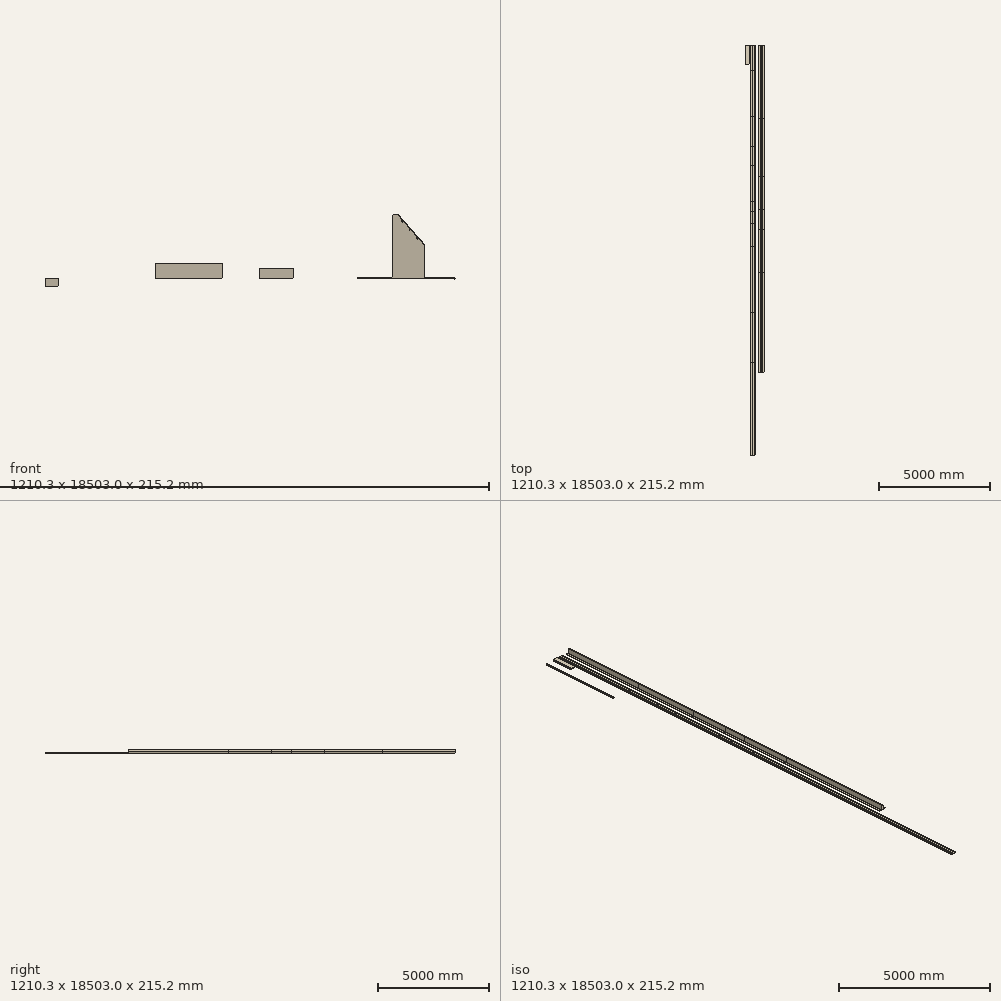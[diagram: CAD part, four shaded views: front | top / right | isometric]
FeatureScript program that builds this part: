
annotation { "Feature Type Name" : "Feature", "Feature Type Description" : "" }
export const myFeature = defineFeature(function(context is Context, id is Id, definition is map)
    precondition{}
    {
        {
            var Q0;
            Q0=qCreatedBy(makeId("Front.planeOp"),FACE);
            var sketch = newSketch(context, id + "F0", { "sketchPlane" : qUnion([Q0])});
            skLineSegment(sketch, "E0", {"start": v(0, 0) * mm, "end": v(105, 0) * mm});
            skLineSegment(sketch, "E1", {"start": v(105, 1) * mm, "end": v(105, 181.45) * mm});
            skLineSegment(sketch, "E2", {"start": v(117.25, 186.07) * mm, "end": v(193, 100) * mm});
            skLineSegment(sketch, "E3", {"start": v(193, 100) * mm, "end": v(193, 0) * mm});
            skLineSegment(sketch, "E4", {"start": v(193, 0) * mm, "end": v(283, 0) * mm});
            skLineSegment(sketch, "E5", {"start": v(283, 0) * mm, "end": v(288, -0.88) * mm});
            skLineSegment(sketch, "E6", {"start": v(288, -0.88) * mm, "end": v(288, 2.12) * mm});
            skLineSegment(sketch, "E7", {"start": v(288, 2.12) * mm, "end": v(283, 3) * mm});
            skLineSegment(sketch, "E8", {"start": v(283, 3) * mm, "end": v(196, 3) * mm});
            skLineSegment(sketch, "E9", {"start": v(196, 3) * mm, "end": v(196, 101.13) * mm});
            skLineSegment(sketch, "E10", {"start": v(196, 101.13) * mm, "end": v(119.5, 188.06) * mm});
            skLineSegment(sketch, "E11", {"start": v(102, 181.45) * mm, "end": v(102, 3) * mm});
            skLineSegment(sketch, "E12", {"start": v(102, 3) * mm, "end": v(0, 3) * mm});
            skLineSegment(sketch, "E13", {"start": v(0, 3) * mm, "end": v(0, 0) * mm});
            skPoint(sketch, "E14.visualSharp", {"position": v(105, 200) * mm});
            skArc(sketch, "E14.filletArc", {"start": v(117.25, 186.07) * mm, "mid": v(109.53, 188) * mm, "end": v(105, 181.45) * mm});
            skPoint(sketch, "E15.visualSharp", {"position": v(102, 207.95) * mm});
            skArc(sketch, "E15.filletArc", {"start": v(119.5, 188.06) * mm, "mid": v(108.47, 190.8) * mm, "end": v(102, 181.45) * mm});
            skLineSegment(sketch, "E16", {"start": v(105, 1) * mm, "end": v(105.5, 1) * mm});
            skLineSegment(sketch, "E17", {"start": v(105.5, 1) * mm, "end": v(105.5, 180.12) * mm});
            skLineSegment(sketch, "E18", {"start": v(117.75, 184.75) * mm, "end": v(192.5, 99.81) * mm});
            skLineSegment(sketch, "E19", {"start": v(192.5, 99.81) * mm, "end": v(192.5, 0) * mm});
            skLineSegment(sketch, "E20", {"start": v(192.5, 0) * mm, "end": v(105, 0) * mm});
            skPoint(sketch, "E21.visualSharp", {"position": v(105.5, 198.67) * mm});
            skArc(sketch, "E21.filletArc", {"start": v(117.75, 184.75) * mm, "mid": v(110.03, 186.67) * mm, "end": v(105.5, 180.12) * mm});
            skSolve(sketch);
        }
        {
            var Q0;
            Q0 = qSketchRegion(id + "F0", true);
            extrude(context, id + "F1", {"entities" : qUnion([Q0]), "depth" : 3300 * mm, "offsetDistance" : 25 * mm});
        }
        {
            var Q0;
            Q0=makeQuery(id+"F1.opExtrude","CAP_FACE",FACE,{"disambiguationData":[OSD([sQuery(id+"F0.wireOp",EDGE,"E0"),sQuery(id+"F0.wireOp",EDGE,"E1"),sQuery(id+"F0.wireOp",EDGE,"E2"),sQuery(id+"F0.wireOp",EDGE,"E3"),sQuery(id+"F0.wireOp",EDGE,"E4"),sQuery(id+"F0.wireOp",EDGE,"E5"),sQuery(id+"F0.wireOp",EDGE,"E6"),sQuery(id+"F0.wireOp",EDGE,"E7"),sQuery(id+"F0.wireOp",EDGE,"E8"),sQuery(id+"F0.wireOp",EDGE,"E9"),sQuery(id+"F0.wireOp",EDGE,"E10"),sQuery(id+"F0.wireOp",EDGE,"E11"),sQuery(id+"F0.wireOp",EDGE,"E12"),sQuery(id+"F0.wireOp",EDGE,"E13"),sQuery(id+"F0.wireOp",EDGE,"E14.filletArc"),sQuery(id+"F0.wireOp",EDGE,"E15.filletArc"),sQuery(id+"F0.wireOp",EDGE,"E16"),sQuery(id+"F0.wireOp",EDGE,"E17"),sQuery(id+"F0.wireOp",EDGE,"E18"),sQuery(id+"F0.wireOp",EDGE,"E19"),sQuery(id+"F0.wireOp",EDGE,"E20"),sQuery(id+"F0.wireOp",EDGE,"E21.filletArc")])],"isStart":false});
            extrude(context, id + "F2", {"entities" : qUnion([Q0]), "depth" : 2600 * mm, "offsetDistance" : 25 * mm});
        }
        {
            var Q0;
            Q0=makeQuery(id+"F2.opExtrude","CAP_FACE",FACE,{"disambiguationData":[OSD([sQuery(id+"F0.wireOp",EDGE,"E0"),sQuery(id+"F0.wireOp",EDGE,"E1"),sQuery(id+"F0.wireOp",EDGE,"E2"),sQuery(id+"F0.wireOp",EDGE,"E3"),sQuery(id+"F0.wireOp",EDGE,"E4"),sQuery(id+"F0.wireOp",EDGE,"E5"),sQuery(id+"F0.wireOp",EDGE,"E6"),sQuery(id+"F0.wireOp",EDGE,"E7"),sQuery(id+"F0.wireOp",EDGE,"E8"),sQuery(id+"F0.wireOp",EDGE,"E9"),sQuery(id+"F0.wireOp",EDGE,"E10"),sQuery(id+"F0.wireOp",EDGE,"E11"),sQuery(id+"F0.wireOp",EDGE,"E12"),sQuery(id+"F0.wireOp",EDGE,"E13"),sQuery(id+"F0.wireOp",EDGE,"E14.filletArc"),sQuery(id+"F0.wireOp",EDGE,"E15.filletArc"),sQuery(id+"F0.wireOp",EDGE,"E16"),sQuery(id+"F0.wireOp",EDGE,"E17"),sQuery(id+"F0.wireOp",EDGE,"E18"),sQuery(id+"F0.wireOp",EDGE,"E19"),sQuery(id+"F0.wireOp",EDGE,"E20"),sQuery(id+"F0.wireOp",EDGE,"E21.filletArc")])],"isStart":false});
            extrude(context, id + "F3", {"entities" : qUnion([Q0]), "depth" : 1500 * mm, "offsetDistance" : 25 * mm});
        }
        {
            var Q0;
            Q0=makeQuery(id+"F3.opExtrude","CAP_FACE",FACE,{"disambiguationData":[OSD([sQuery(id+"F0.wireOp",EDGE,"E0"),sQuery(id+"F0.wireOp",EDGE,"E1"),sQuery(id+"F0.wireOp",EDGE,"E2"),sQuery(id+"F0.wireOp",EDGE,"E3"),sQuery(id+"F0.wireOp",EDGE,"E4"),sQuery(id+"F0.wireOp",EDGE,"E5"),sQuery(id+"F0.wireOp",EDGE,"E6"),sQuery(id+"F0.wireOp",EDGE,"E7"),sQuery(id+"F0.wireOp",EDGE,"E8"),sQuery(id+"F0.wireOp",EDGE,"E9"),sQuery(id+"F0.wireOp",EDGE,"E10"),sQuery(id+"F0.wireOp",EDGE,"E11"),sQuery(id+"F0.wireOp",EDGE,"E12"),sQuery(id+"F0.wireOp",EDGE,"E13"),sQuery(id+"F0.wireOp",EDGE,"E14.filletArc"),sQuery(id+"F0.wireOp",EDGE,"E15.filletArc"),sQuery(id+"F0.wireOp",EDGE,"E16"),sQuery(id+"F0.wireOp",EDGE,"E17"),sQuery(id+"F0.wireOp",EDGE,"E18"),sQuery(id+"F0.wireOp",EDGE,"E19"),sQuery(id+"F0.wireOp",EDGE,"E20"),sQuery(id+"F0.wireOp",EDGE,"E21.filletArc")])],"isStart":false});
            extrude(context, id + "F4", {"entities" : qUnion([Q0]), "depth" : 900 * mm, "offsetDistance" : 25 * mm});
        }
        {
            var Q0;
            Q0=qCreatedBy(makeId("Front.planeOp"),FACE);
            var sketch = newSketch(context, id + "F5", { "sketchPlane" : qUnion([Q0])});
            skLineSegment(sketch, "E22", {"start": v(-141.12, 0) * mm, "end": v(-341.12, 0) * mm});
            skLineSegment(sketch, "E23", {"start": v(-341.12, 0) * mm, "end": v(-341.12, 2) * mm});
            skLineSegment(sketch, "E24", {"start": v(-341.12, 2) * mm, "end": v(-291.12, 2) * mm});
            skLineSegment(sketch, "E25", {"start": v(-291.12, 2) * mm, "end": v(-291.12, 32) * mm});
            skLineSegment(sketch, "E26", {"start": v(-291.12, 32) * mm, "end": v(-191.12, 32) * mm});
            skLineSegment(sketch, "E27", {"start": v(-191.12, 32) * mm, "end": v(-191.12, 2) * mm});
            skLineSegment(sketch, "E28", {"start": v(-191.12, 2) * mm, "end": v(-141.12, 2) * mm});
            skLineSegment(sketch, "E29", {"start": v(-141.12, 2) * mm, "end": v(-141.12, 0) * mm});
            skSolve(sketch);
        }
        {
            var Q0;
            Q0 = qSketchRegion(id + "F5", true);
            extrude(context, id + "F6", {"entities" : qUnion([Q0]), "depth" : 1125 * mm, "offsetDistance" : 25 * mm});
        }
        {
            var Q0;
            Q0=makeQuery(id+"F6.opExtrude","CAP_FACE",FACE,{"disambiguationData":[OSD([sQuery(id+"F5.wireOp",EDGE,"E22"),sQuery(id+"F5.wireOp",EDGE,"E23"),sQuery(id+"F5.wireOp",EDGE,"E24"),sQuery(id+"F5.wireOp",EDGE,"E25"),sQuery(id+"F5.wireOp",EDGE,"E26"),sQuery(id+"F5.wireOp",EDGE,"E27"),sQuery(id+"F5.wireOp",EDGE,"E28"),sQuery(id+"F5.wireOp",EDGE,"E29")])],"isStart":false});
            extrude(context, id + "F7", {"entities" : qUnion([Q0]), "depth" : 2100 * mm, "offsetDistance" : 25 * mm});
        }
        {
            var Q0;
            Q0=makeQuery(id+"F7.opExtrude","CAP_FACE",FACE,{"disambiguationData":[OSD([sQuery(id+"F5.wireOp",EDGE,"E22"),sQuery(id+"F5.wireOp",EDGE,"E23"),sQuery(id+"F5.wireOp",EDGE,"E24"),sQuery(id+"F5.wireOp",EDGE,"E25"),sQuery(id+"F5.wireOp",EDGE,"E26"),sQuery(id+"F5.wireOp",EDGE,"E27"),sQuery(id+"F5.wireOp",EDGE,"E28"),sQuery(id+"F5.wireOp",EDGE,"E29")])],"isStart":false});
            extrude(context, id + "F8", {"entities" : qUnion([Q0]), "depth" : 1350 * mm, "offsetDistance" : 25 * mm});
        }
        {
            var Q0;
            Q0=makeQuery(id+"F8.opExtrude","CAP_FACE",FACE,{"disambiguationData":[OSD([sQuery(id+"F5.wireOp",EDGE,"E22"),sQuery(id+"F5.wireOp",EDGE,"E23"),sQuery(id+"F5.wireOp",EDGE,"E24"),sQuery(id+"F5.wireOp",EDGE,"E25"),sQuery(id+"F5.wireOp",EDGE,"E26"),sQuery(id+"F5.wireOp",EDGE,"E27"),sQuery(id+"F5.wireOp",EDGE,"E28"),sQuery(id+"F5.wireOp",EDGE,"E29")])],"isStart":false});
            extrude(context, id + "F9", {"entities" : qUnion([Q0]), "depth" : 825 * mm, "offsetDistance" : 25 * mm});
        }
        {
            var Q0;
            Q0=makeQuery(id+"F9.opExtrude","CAP_FACE",FACE,{"disambiguationData":[OSD([sQuery(id+"F5.wireOp",EDGE,"E22"),sQuery(id+"F5.wireOp",EDGE,"E23"),sQuery(id+"F5.wireOp",EDGE,"E24"),sQuery(id+"F5.wireOp",EDGE,"E25"),sQuery(id+"F5.wireOp",EDGE,"E26"),sQuery(id+"F5.wireOp",EDGE,"E27"),sQuery(id+"F5.wireOp",EDGE,"E28"),sQuery(id+"F5.wireOp",EDGE,"E29")])],"isStart":false});
            extrude(context, id + "F10", {"entities" : qUnion([Q0]), "depth" : 1650 * mm, "offsetDistance" : 25 * mm});
        }
        {
            var Q0;
            Q0=makeQuery(id+"F10.opExtrude","CAP_FACE",FACE,{"disambiguationData":[OSD([sQuery(id+"F5.wireOp",EDGE,"E22"),sQuery(id+"F5.wireOp",EDGE,"E23"),sQuery(id+"F5.wireOp",EDGE,"E24"),sQuery(id+"F5.wireOp",EDGE,"E25"),sQuery(id+"F5.wireOp",EDGE,"E26"),sQuery(id+"F5.wireOp",EDGE,"E27"),sQuery(id+"F5.wireOp",EDGE,"E28"),sQuery(id+"F5.wireOp",EDGE,"E29")])],"isStart":false});
            extrude(context, id + "F11", {"entities" : qUnion([Q0]), "depth" : 420 * mm, "offsetDistance" : 25 * mm});
        }
        {
            var Q0;
            Q0=makeQuery(id+"F11.opExtrude","CAP_FACE",FACE,{"disambiguationData":[OSD([sQuery(id+"F5.wireOp",EDGE,"E22"),sQuery(id+"F5.wireOp",EDGE,"E23"),sQuery(id+"F5.wireOp",EDGE,"E24"),sQuery(id+"F5.wireOp",EDGE,"E25"),sQuery(id+"F5.wireOp",EDGE,"E26"),sQuery(id+"F5.wireOp",EDGE,"E27"),sQuery(id+"F5.wireOp",EDGE,"E28"),sQuery(id+"F5.wireOp",EDGE,"E29")])],"isStart":false});
            extrude(context, id + "F12", {"entities" : qUnion([Q0]), "depth" : 583 * mm, "offsetDistance" : 25 * mm});
        }
        {
            var Q0;
            Q0=makeQuery(id+"F12.opExtrude","CAP_FACE",FACE,{"disambiguationData":[OSD([sQuery(id+"F5.wireOp",EDGE,"E22"),sQuery(id+"F5.wireOp",EDGE,"E23"),sQuery(id+"F5.wireOp",EDGE,"E24"),sQuery(id+"F5.wireOp",EDGE,"E25"),sQuery(id+"F5.wireOp",EDGE,"E26"),sQuery(id+"F5.wireOp",EDGE,"E27"),sQuery(id+"F5.wireOp",EDGE,"E28"),sQuery(id+"F5.wireOp",EDGE,"E29")])],"isStart":false});
            extrude(context, id + "F13", {"entities" : qUnion([Q0]), "depth" : 1000 * mm, "offsetDistance" : 25 * mm});
        }
        {
            var Q0;
            Q0=makeQuery(id+"F13.opExtrude","CAP_FACE",FACE,{"disambiguationData":[OSD([sQuery(id+"F5.wireOp",EDGE,"E22"),sQuery(id+"F5.wireOp",EDGE,"E23"),sQuery(id+"F5.wireOp",EDGE,"E24"),sQuery(id+"F5.wireOp",EDGE,"E25"),sQuery(id+"F5.wireOp",EDGE,"E26"),sQuery(id+"F5.wireOp",EDGE,"E27"),sQuery(id+"F5.wireOp",EDGE,"E28"),sQuery(id+"F5.wireOp",EDGE,"E29")])],"isStart":false});
            extrude(context, id + "F14", {"entities" : qUnion([Q0]), "depth" : 3000 * mm, "offsetDistance" : 25 * mm});
        }
        {
            var Q0;
            Q0=qCreatedBy(makeId("Front.planeOp"),FACE);
            var sketch = newSketch(context, id + "F15", { "sketchPlane" : qUnion([Q0])});
            skLineSegment(sketch, "E30.bottom", {"start": v(-597, 0) * mm, "end": v(-400, 0) * mm});
            skLineSegment(sketch, "E30.top", {"start": v(-597, 44) * mm, "end": v(-400, 44) * mm});
            skLineSegment(sketch, "E30.left", {"start": v(-597, 0) * mm, "end": v(-597, 44) * mm});
            skLineSegment(sketch, "E30.right", {"start": v(-400, 0) * mm, "end": v(-400, 44) * mm});
            skSolve(sketch);
        }
        {
            var Q0;
            Q0 = qSketchRegion(id + "F15", true);
            extrude(context, id + "F16", {"entities" : qUnion([Q0]), "depth" : 840 * mm, "offsetDistance" : 25 * mm});
        }
        {
            var Q0;
            Q0=qCreatedBy(makeId("Front.planeOp"),FACE);
            var sketch = newSketch(context, id + "F17", { "sketchPlane" : qUnion([Q0])});
            skLineSegment(sketch, "E31.bottom", {"start": v(-922.31, 1.25) * mm, "end": v(-884.31, 1.25) * mm});
            skLineSegment(sketch, "E31.top", {"start": v(-922.31, -23.75) * mm, "end": v(-884.31, -23.75) * mm});
            skLineSegment(sketch, "E31.left", {"start": v(-922.31, 1.25) * mm, "end": v(-922.31, -23.75) * mm});
            skLineSegment(sketch, "E31.right", {"start": v(-884.31, 1.25) * mm, "end": v(-884.31, -23.75) * mm});
            skSolve(sketch);
        }
        {
            var Q0;
            Q0 = qSketchRegion(id + "F17", true);
            extrude(context, id + "F18", {"entities" : qUnion([Q0]), "depth" : 1193 * mm, "offsetDistance" : 25 * mm});
        }
        {
            var Q0;
            Q0=makeQuery(id+"F18.opExtrude","CAP_FACE",FACE,{"disambiguationData":[OSD([sQuery(id+"F17.wireOp",EDGE,"E31.bottom"),sQuery(id+"F17.wireOp",EDGE,"E31.top"),sQuery(id+"F17.wireOp",EDGE,"E31.left"),sQuery(id+"F17.wireOp",EDGE,"E31.right")])],"isStart":false});
            extrude(context, id + "F19", {"entities" : qUnion([Q0]), "depth" : 937 * mm, "offsetDistance" : 25 * mm});
        }
        {
            var Q0;
            Q0=makeQuery(id+"F19.opExtrude","CAP_FACE",FACE,{"disambiguationData":[OSD([sQuery(id+"F17.wireOp",EDGE,"E31.bottom"),sQuery(id+"F17.wireOp",EDGE,"E31.top"),sQuery(id+"F17.wireOp",EDGE,"E31.left"),sQuery(id+"F17.wireOp",EDGE,"E31.right")])],"isStart":false});
            extrude(context, id + "F20", {"entities" : qUnion([Q0]), "depth" : 1047 * mm, "offsetDistance" : 25 * mm});
        }
        {
            var Q0;
            Q0=makeQuery(id+"F14.opExtrude","CAP_FACE",FACE,{"disambiguationData":[OSD([sQuery(id+"F5.wireOp",EDGE,"E22"),sQuery(id+"F5.wireOp",EDGE,"E23"),sQuery(id+"F5.wireOp",EDGE,"E24"),sQuery(id+"F5.wireOp",EDGE,"E25"),sQuery(id+"F5.wireOp",EDGE,"E26"),sQuery(id+"F5.wireOp",EDGE,"E27"),sQuery(id+"F5.wireOp",EDGE,"E28"),sQuery(id+"F5.wireOp",EDGE,"E29")])],"isStart":false});
            extrude(context, id + "F21", {"entities" : qUnion([Q0]), "depth" : 2250 * mm, "offsetDistance" : 25 * mm});
        }
        {
            var Q0;
            Q0=makeQuery(id+"F21.opExtrude","CAP_FACE",FACE,{"disambiguationData":[OSD([sQuery(id+"F5.wireOp",EDGE,"E22"),sQuery(id+"F5.wireOp",EDGE,"E23"),sQuery(id+"F5.wireOp",EDGE,"E24"),sQuery(id+"F5.wireOp",EDGE,"E25"),sQuery(id+"F5.wireOp",EDGE,"E26"),sQuery(id+"F5.wireOp",EDGE,"E27"),sQuery(id+"F5.wireOp",EDGE,"E28"),sQuery(id+"F5.wireOp",EDGE,"E29")])],"isStart":false});
            extrude(context, id + "F22", {"entities" : qUnion([Q0]), "depth" : 4200 * mm, "offsetDistance" : 25 * mm});
        }
        {
            var Q0;
            Q0=makeQuery(id+"F4.opExtrude","CAP_FACE",FACE,{"disambiguationData":[OSD([sQuery(id+"F0.wireOp",EDGE,"E0"),sQuery(id+"F0.wireOp",EDGE,"E1"),sQuery(id+"F0.wireOp",EDGE,"E2"),sQuery(id+"F0.wireOp",EDGE,"E3"),sQuery(id+"F0.wireOp",EDGE,"E4"),sQuery(id+"F0.wireOp",EDGE,"E5"),sQuery(id+"F0.wireOp",EDGE,"E6"),sQuery(id+"F0.wireOp",EDGE,"E7"),sQuery(id+"F0.wireOp",EDGE,"E8"),sQuery(id+"F0.wireOp",EDGE,"E9"),sQuery(id+"F0.wireOp",EDGE,"E10"),sQuery(id+"F0.wireOp",EDGE,"E11"),sQuery(id+"F0.wireOp",EDGE,"E12"),sQuery(id+"F0.wireOp",EDGE,"E13"),sQuery(id+"F0.wireOp",EDGE,"E14.filletArc"),sQuery(id+"F0.wireOp",EDGE,"E15.filletArc"),sQuery(id+"F0.wireOp",EDGE,"E16"),sQuery(id+"F0.wireOp",EDGE,"E17"),sQuery(id+"F0.wireOp",EDGE,"E18"),sQuery(id+"F0.wireOp",EDGE,"E19"),sQuery(id+"F0.wireOp",EDGE,"E20"),sQuery(id+"F0.wireOp",EDGE,"E21.filletArc")])],"isStart":false});
            extrude(context, id + "F23", {"entities" : qUnion([Q0]), "depth" : 1950 * mm, "offsetDistance" : 25 * mm});
        }
        {
            var Q0;
            Q0=makeQuery(id+"F23.opExtrude","CAP_FACE",FACE,{"disambiguationData":[OSD([sQuery(id+"F0.wireOp",EDGE,"E0"),sQuery(id+"F0.wireOp",EDGE,"E1"),sQuery(id+"F0.wireOp",EDGE,"E2"),sQuery(id+"F0.wireOp",EDGE,"E3"),sQuery(id+"F0.wireOp",EDGE,"E4"),sQuery(id+"F0.wireOp",EDGE,"E5"),sQuery(id+"F0.wireOp",EDGE,"E6"),sQuery(id+"F0.wireOp",EDGE,"E7"),sQuery(id+"F0.wireOp",EDGE,"E8"),sQuery(id+"F0.wireOp",EDGE,"E9"),sQuery(id+"F0.wireOp",EDGE,"E10"),sQuery(id+"F0.wireOp",EDGE,"E11"),sQuery(id+"F0.wireOp",EDGE,"E12"),sQuery(id+"F0.wireOp",EDGE,"E13"),sQuery(id+"F0.wireOp",EDGE,"E14.filletArc"),sQuery(id+"F0.wireOp",EDGE,"E15.filletArc"),sQuery(id+"F0.wireOp",EDGE,"E16"),sQuery(id+"F0.wireOp",EDGE,"E17"),sQuery(id+"F0.wireOp",EDGE,"E18"),sQuery(id+"F0.wireOp",EDGE,"E19"),sQuery(id+"F0.wireOp",EDGE,"E20"),sQuery(id+"F0.wireOp",EDGE,"E21.filletArc")])],"isStart":false});
            extrude(context, id + "F24", {"entities" : qUnion([Q0]), "depth" : 4500 * mm, "offsetDistance" : 25 * mm});
        }
    });
